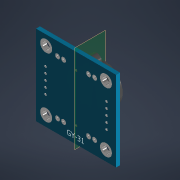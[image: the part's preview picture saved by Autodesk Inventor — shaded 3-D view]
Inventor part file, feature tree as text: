
AUTODESK INVENTOR PART (.ipt)
format: ipt  version: 2021 (Build 250183000, 183)  size: 1,512,960 bytes
history: native  units: mm
features: sketch x20, extrude x14, projected_geometry x8, hole x4, mirror x4, fillet x2, thread x1, plane x1
ambient origin geometry x8: Origin, YZ Plane, XZ Plane, XY Plane, X Axis, Y Axis, Z Axis, Center Point
bodies: Solid1 (feature_tree)
feature tree (54):
  extrude  "Extrusion1"  Depth=33.5mm
  hole  "Hole1"  [1 undecoded]
  extrude  "Extrusion2"  Depth=25.0mm
  extrude  "Extrusion3"  TaperAngle=0.0deg  [1 undecoded]
  hole  "Hole2"  [1 undecoded]
  mirror  "Mirror1"
  extrude  "Extrusion4"  Depth=5.0mm
  mirror  "Mirror2"
  extrude  "Extrusion5"  Depth=5.0mm
  mirror  "Mirror3"
  extrude  "Extrusion6"  Depth=0.01mm TaperAngle=0.0deg
  extrude  "Extrusion7"  Depth=4.0mm
  hole  "Hole3"  [1 undecoded]
  extrude  "Extrusion8"  Depth=2.0mm
  extrude  "Extrusion9"  Depth=2.0mm
  mirror  "Mirror4"
  extrude  "Extrusion10"  Depth=0.01mm TaperAngle=0.0deg
  extrude  "Extrusion11"  Depth=13.0mm
  hole  "Hole4"  [1 undecoded]
  extrude  "Extrusion12"  Depth=0.01mm TaperAngle=0.0deg
  fillet  "Fillet1"  Radius=0.01mm
  fillet  "Fillet2"  Radius=2.54mm
  extrude  "Extrusion13"  Depth=9.0mm
  extrude  "Extrusion14"  Depth=5.5mm
  sketch  "Sketch19"  dims[d62=2.54mm d63=5.5mm d64=9.0mm]
  sketch  "Sketch20"  dims[d65=1.0mm d66=6.0mm d67=4.0mm d68=2.0mm d69=90.0deg d70=8.0mm d71=20.594885mm d72=2.0mm d73=2.0mm d74=2.0mm d75=2.0mm d76=0.01mm d77=0.0mm d78=2.0mm d79=2.0mm d80=2.0mm d81=2.0mm d82=0.01mm d83=0.0mm d84=16.0mm d85=16.0mm d86=10.0mm d87=4.3mm d88=7.0mm d89=0.0mm d90=15.8mm d91=3.0mm d92=0.0mm d93=1.0mm d94=6.0mm d95=4.0mm d96=2.0mm d97=90.0deg d98=8.0mm d99=20.594885mm d100=3.5mm d101=0.9mm d102=1.5mm d103=0.0mm d104=0.0mm d105=0.02mm d106=0.02mm d107=2.14mm d108=0.9mm d109=0.0mm d111=1.0mm d112=1.0mm d113=6.4mm d114=0.0mm d115=10.0mm d116=0.0mm]
  thread  "Thread1"  [1 undecoded]
  sketch  "Sketch1"  dims[d0=33.5mm d1=33.5mm]
  sketch  "Sketch2"  dims[d2=1.65mm d3=0.0mm d4=25.0mm]
  sketch  "Sketch3"  dims[d5=25.0mm d6=25.0mm]
  projected_geometry  "Projected Loop1"
  sketch  "Sketch4"  dims[d7=25.0mm d8=0.0mm]
  projected_geometry  "Projected Loop2"
  sketch  "Sketch5"  dims[d9=4.25mm d10=4.25mm]
  plane  "Work Plane1"
  sketch  "Sketch6"  dims[d11=3.0mm d12=6.0mm d13=4.0mm d14=2.0mm d15=90.0deg d16=8.0mm d17=20.594885mm d18=5.0mm]
  projected_geometry  "Projected Loop3"
  sketch  "Sketch7"  dims[d19=5.0mm d20=5.0mm]
  sketch  "Sketch8"  dims[d21=5.0mm d22=0.01mm d23=0.0mm]
  sketch  "Sketch9"  dims[d24=0.01mm d25=0.0mm d26=4.0mm]
  sketch  "Sketch10"  dims[d27=50.0mm d29=2.54mm d30=10.0mm d32=10.0mm]
  sketch  "Sketch11"  dims[d34=1.0mm d35=6.0mm d36=4.0mm d37=2.0mm d38=90.0deg d39=8.0mm d40=20.594885mm d41=11.68mm]
  projected_geometry  "Projected Loop4"
  sketch  "Sketch12"  dims[d42=2.0mm d43=2.0mm]
  projected_geometry  "Projected Loop5"
  sketch  "Sketch13"  dims[d44=2.0mm d45=2.0mm]
  sketch  "Sketch14"  dims[d46=2.0mm d47=0.01mm d48=0.0mm]
  sketch  "Sketch15"  dims[d49=3.3mm d50=13.0mm]
  projected_geometry  "Projected Loop6"
  sketch  "Sketch16"  dims[d51=0.4mm d52=0.4mm]
  sketch  "Sketch17"  dims[d53=0.01mm d54=0.0mm d55=0.01mm d56=0.0mm d57=0.01mm d58=0.0mm d59=2.54mm]
  sketch  "Sketch18"  dims[d60=5.5mm d61=9.0mm]
  projected_geometry  "Projected Loop7"
  projected_geometry  "Projected Loop8"
note: 6 required parameter values undecoded (feature->parameter linkage not recoverable at this tier; creation-order binding heuristic only, values carry confidence <= 0.55)
